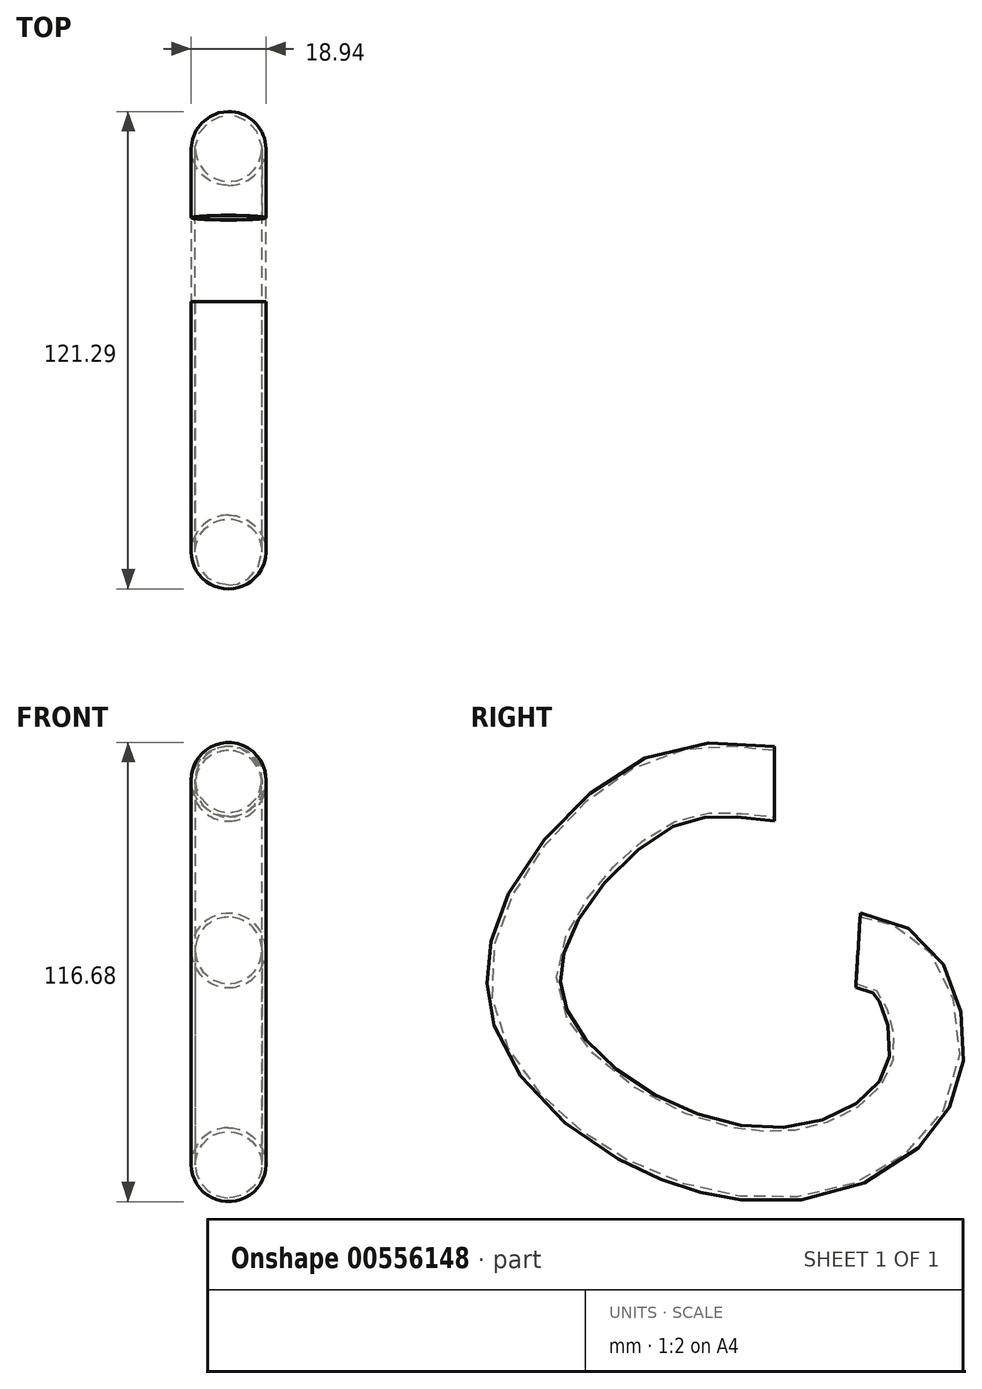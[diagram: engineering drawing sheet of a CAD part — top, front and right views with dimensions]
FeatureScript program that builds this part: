
annotation { "Feature Type Name" : "Feature", "Feature Type Description" : "" }
export const myFeature = defineFeature(function(context is Context, id is Id, definition is map)
    precondition{}
    {
        {
            var Q0;
            Q0=qCreatedBy(makeId("Front.planeOp"),FACE);
            var sketch = newSketch(context, id + "F0", { "sketchPlane" : qUnion([Q0])});
            skCircle(sketch, "E0", {"center": v(0, 56.12) * mm, "radius": 9.47 * mm});
            skSolve(sketch);
        }
        {
            var Q0;
            Q0=qCreatedBy(makeId("Right.planeOp"),FACE);
            var sketch = newSketch(context, id + "F1", { "sketchPlane" : qUnion([Q0])});
            skFitSpline(sketch, "E1", {"points": [v(0, 56.12) * mm, v(-28.2, 54.4) * mm, v(-59.29, 23.6) * mm, v(-61.01, -5.47) * mm, v(-32.23, -32.52) * mm, v(10.65, -39.43) * mm, v(37.7, -18.13) * mm, v(32.52, 8.63) * mm, v(21.3, 13.81) * mm], "startDerivative": vector(-233.9, 29.75) * mm, "endDerivative": vector(-152.03, 29.13) * mm});
            skSolve(sketch);
        }
        {
            var Q0;
            Q0 = qSketchRegion(id + "F0", true);
            var Q1;
            Q1 = qConstructionFilter(qBodyType(qCreatedBy(id + "F1" ,EDGE), BodyType.WIRE), ConstructionObject.NO);
            sweep(context, id + "F2", {"profiles" : qUnion([Q0]), "path" : qUnion([Q1])});
        }
        {
            var Q0;
            Q0=makeQuery(id+"F2.opSweep","CAP_FACE",FACE,{"disambiguationData":[OSD([sQuery(id+"F0.wireOp",EDGE,"E0"),sQuery(id+"F1.wireOp",VERTEX,"E1.start")])],"isStart":true});
            var Q1;
            Q1=makeQuery(id+"F2.opSweep","CAP_FACE",FACE,{"disambiguationData":[OSD([sQuery(id+"F0.wireOp",EDGE,"E0"),sQuery(id+"F1.wireOp",VERTEX,"E1.end")])],"isStart":false});
            shell(context, id + "F3", {"entities" : qUnion([Q0, Q1]), "thickness" : 1 * mm});
        }
    });
